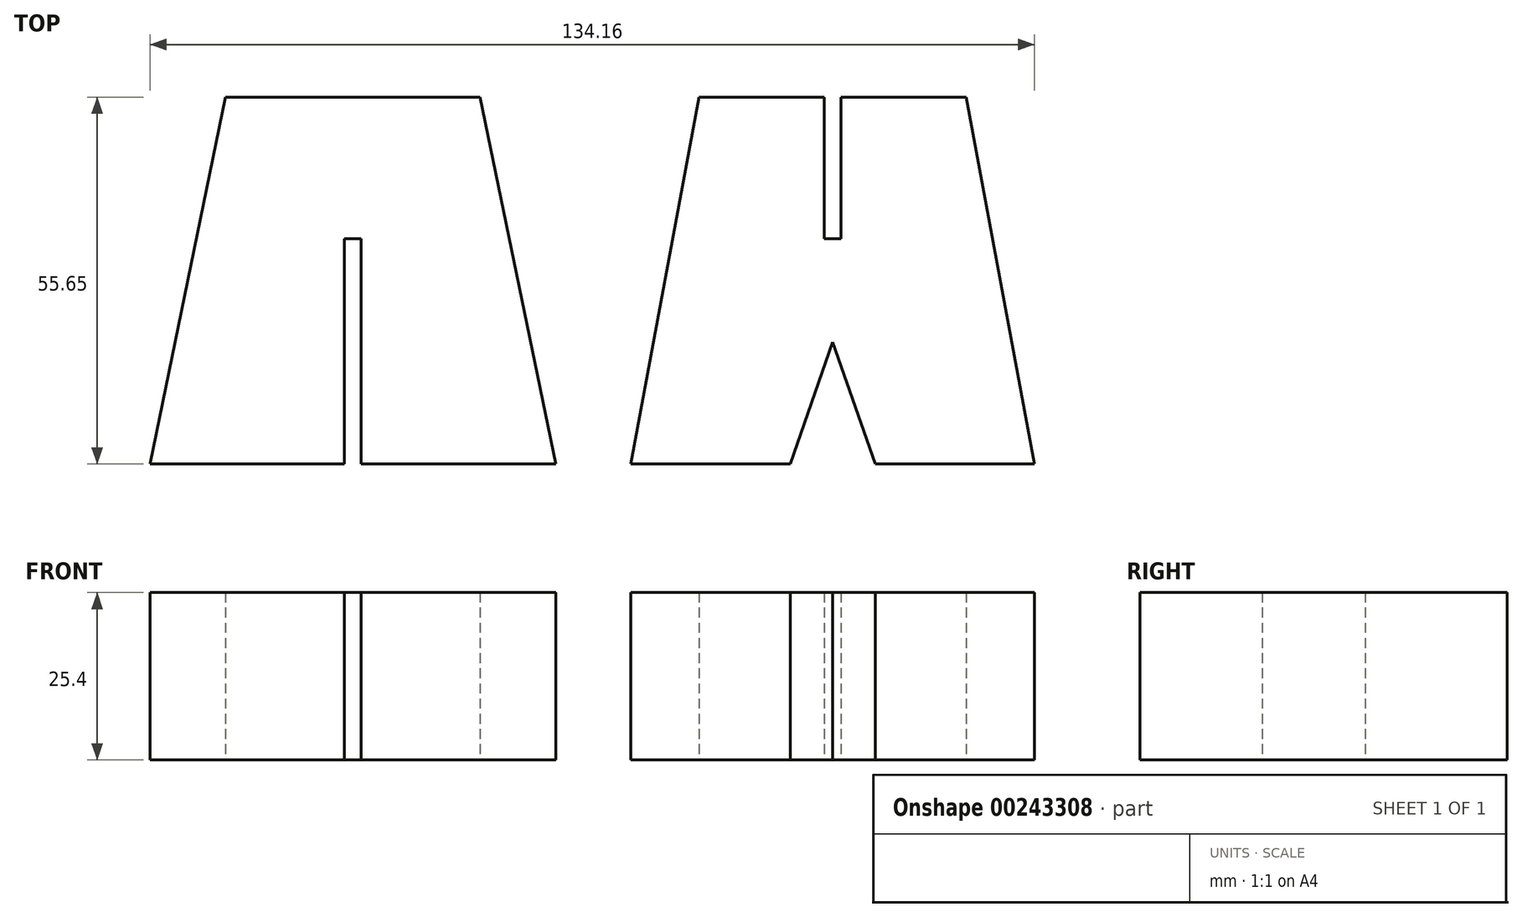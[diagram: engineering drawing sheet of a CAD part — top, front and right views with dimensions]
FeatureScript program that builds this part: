
annotation { "Feature Type Name" : "Feature", "Feature Type Description" : "" }
export const myFeature = defineFeature(function(context is Context, id is Id, definition is map)
    precondition{}
    {
        {
            var Q0;
            Q0=qCreatedBy(makeId("Top.planeOp"),FACE);
            var sketch = newSketch(context, id + "F0", { "sketchPlane" : qUnion([Q0])});
            skLineSegment(sketch, "E0", {"start": v(-19.76, 55.65) * mm, "end": v(-58.4, 55.65) * mm});
            skLineSegment(sketch, "E1", {"start": v(-58.4, 55.65) * mm, "end": v(-69.84, 0) * mm});
            skLineSegment(sketch, "E2", {"start": v(-69.84, 0) * mm, "end": v(-40.35, 0) * mm});
            skLineSegment(sketch, "E3", {"start": v(-40.35, 0) * mm, "end": v(-40.35, 34.16) * mm});
            skLineSegment(sketch, "E4", {"start": v(-40.35, 34.16) * mm, "end": v(-37.8, 34.16) * mm});
            skLineSegment(sketch, "E5", {"start": v(-37.8, 34.16) * mm, "end": v(-37.8, 0) * mm});
            skLineSegment(sketch, "E6", {"start": v(-37.8, 0) * mm, "end": v(-8.31, 0) * mm});
            skLineSegment(sketch, "E7", {"start": v(-8.31, 0) * mm, "end": v(-19.76, 55.65) * mm});
            skLineSegment(sketch, "E8", {"start": v(3.07, 0) * mm, "end": v(27.25, 0) * mm});
            skLineSegment(sketch, "E9", {"start": v(27.25, 0) * mm, "end": v(33.7, 18.52) * mm});
            skLineSegment(sketch, "E10", {"start": v(33.7, 18.52) * mm, "end": v(40.15, 0) * mm});
            skLineSegment(sketch, "E11", {"start": v(40.15, 0) * mm, "end": v(64.32, 0) * mm});
            skLineSegment(sketch, "E12", {"start": v(64.32, 0) * mm, "end": v(53.96, 55.64) * mm});
            skLineSegment(sketch, "E13", {"start": v(53.96, 55.64) * mm, "end": v(34.97, 55.64) * mm});
            skLineSegment(sketch, "E14", {"start": v(34.97, 55.64) * mm, "end": v(34.97, 34.15) * mm});
            skLineSegment(sketch, "E15", {"start": v(34.97, 34.15) * mm, "end": v(32.43, 34.15) * mm});
            skLineSegment(sketch, "E16", {"start": v(32.43, 34.15) * mm, "end": v(32.43, 55.64) * mm});
            skLineSegment(sketch, "E17", {"start": v(32.43, 55.64) * mm, "end": v(13.43, 55.64) * mm});
            skLineSegment(sketch, "E18", {"start": v(13.43, 55.64) * mm, "end": v(3.07, 0) * mm});
            skSolve(sketch);
        }
        {
            var Q0;
            Q0=makeQuery(id+"F0.imprint","IMPRINT",FACE,{"disambiguationData":[TD([[makeQuery(id+"F0.imprint","IMPRINT",EDGE,{"derivedFrom":sQuery(id+"F0.wireOp",EDGE,"E0")}),1.0]])]});
            var Q1;
            Q1=makeQuery(id+"F0.imprint","IMPRINT",FACE,{"disambiguationData":[TD([[makeQuery(id+"F0.imprint","IMPRINT",EDGE,{"derivedFrom":sQuery(id+"F0.wireOp",EDGE,"E8")}),1.0]])]});
            extrude(context, id + "F1", {"entities" : qUnion([Q0, Q1]), "depth" : 25.4 * mm});
        }
    });
